# Revit family: Heater-BERKO-Explosion_Proof_Unit
name_source: partatom
category: Mechanical Equipment
units: mm (PartAtom-declared; Revit-internal decimal feet)

## family parameters
Classification = None
Cut with Voids When Loaded = No
Host = Face
Part Type = Normal
Room Calculation Point = No
Round Connector Dimension = Use Diameter
Shared = No

## types (67) — shared parameters
Default Elevation = 4' - 0"
Description = Proof Unit Heater
Frame Size 1 = Yes
Instruction Sheet Link = https://www.marleymep.com
Manufacturer = Marley® Engineered Products
Material = Berko - Stainless Steel - Beige
Number of Poles = 1
Power Factor = 1
Product Documentation Link = https://www.marleymep.com
Product Name = RUX Series Explosion-Proof Unit Heater Gen2
Product Page URL = https://www.marleymep.com
URL = https://www.marleymep.com
Version = 2020 - v1.0a

## per-type parameters (varying)
| type | Actual Supply Air Flow | Air Flow - Throw | Amps | Classification | Depth | Fan Blade Diameter | Frame Size 2 | Frame Size 3 | Frequency | Height | Length | MH Height | MW Height | Motor HP | Motor RPM | Phase | Shipping Weight | Total Heating Capacity | Voltage | Watts |
| RUX-233-FA-0036C | 650 CFM | 1' - 3" | 17 A | 60 Hz Models/Class I, Divisions 1 and 2, Groups C & D/Class II, Divisions 1 and 2, Groups E, F & G/Class I, Zones 1 and 2, Group II | 1' - 4 1/16" | 1' - 0" | No | No | 60 Hz | 1' - 7 3/8" | 1' - 9 3/4" | 0' - 11 1/16" | 0' - 9" | 0.25 | 1725 RPM | 1 | 130 lbs | 10236.0 Btu/h | 208 V | 3000 W |
| RUX-233-FA-0036J | 650 CFM | 1' - 3" | 15 A | 60 Hz Models/Class I, Divisions 1 and 2, Groups C & D/Class II, Divisions 1 and 2, Groups E, F & G/Class I, Zones 1 and 2, Group II | 1' - 4 1/16" | 1' - 0" | No | No | 60 Hz | 1' - 7 3/8" | 1' - 9 3/4" | 0' - 11 1/16" | 0' - 9" | 0.25 | 1725 RPM | 1 | 130 lbs | 10236.0 Btu/h | 240 V | 3000 W |
| RUX-233-FA-0036D | 650 CFM | 1' - 3" | 10 A | 60 Hz Models/Class I, Divisions 1 and 2, Groups C & D/Class II, Divisions 1 and 2, Groups E, F & G/Class I, Zones 1 and 2, Group II | 1' - 4 1/16" | 1' - 0" | No | No | 60 Hz | 1' - 7 3/8" | 1' - 9 3/4" | 0' - 11 1/16" | 0' - 9" | 0.25 | 1725 RPM | 3 | 130 lbs | 10236.0 Btu/h | 208 V | 3000 W |
| RUX-233-FA-0036K | 650 CFM | 1' - 3" | 9 A | 60 Hz Models/Class I, Divisions 1 and 2, Groups C & D/Class II, Divisions 1 and 2, Groups E, F & G/Class I, Zones 1 and 2, Group II | 1' - 4 1/16" | 1' - 0" | No | No | 60 Hz | 1' - 7 3/8" | 1' - 9 3/4" | 0' - 11 1/16" | 0' - 9" | 0.25 | 1725 RPM | 3 | 130 lbs | 10236.0 Btu/h | 240 V | 3000 W |
| RUX-233-FA-0036U | 650 CFM | 1' - 3" | 5 A | 60 Hz Models/Class I, Divisions 1 and 2, Groups C & D/Class II, Divisions 1 and 2, Groups E, F & G/Class I, Zones 1 and 2, Group II | 1' - 4 1/16" | 1' - 0" | No | No | 60 Hz | 1' - 7 3/8" | 1' - 9 3/4" | 0' - 11 1/16" | 0' - 9" | 0.25 | 1725 RPM | 3 | 130 lbs | 10236.0 Btu/h | 480 V | 3000 W |
| RUX-233-FA-0036Z | 650 CFM | 1' - 3" | 4 A | 60 Hz Models/Class I, Divisions 1 and 2, Groups C & D/Class II, Divisions 1 and 2, Groups E, F & G/Class I, Zones 1 and 2, Group II | 1' - 4 1/16" | 1' - 0" | No | No | 60 Hz | 1' - 7 3/8" | 1' - 9 3/4" | 0' - 11 1/16" | 0' - 9" | 0.25 | 1725 RPM | 3 | 130 lbs | 10236.0 Btu/h | 600 V | 3000 W |
| RUX-233-FA-0056C | 650 CFM | 1' - 3" | 26 A | 60 Hz Models/Class I, Divisions 1 and 2, Groups C & D/Class II, Divisions 1 and 2, Groups E, F & G/Class I, Zones 1 and 2, Group II | 1' - 4 1/16" | 1' - 0" | No | No | 60 Hz | 1' - 7 3/8" | 1' - 9 3/4" | 0' - 11 1/16" | 0' - 9" | 0.25 | 1725 RPM | 1 | 130 lbs | 17060.0 Btu/h | 208 V | 5000 W |
| RUX-233-FA-0056J | 650 CFM | 1' - 3" | 23 A | 60 Hz Models/Class I, Divisions 1 and 2, Groups C & D/Class II, Divisions 1 and 2, Groups E, F & G/Class I, Zones 1 and 2, Group II | 1' - 4 1/16" | 1' - 0" | No | No | 60 Hz | 1' - 7 3/8" | 1' - 9 3/4" | 0' - 11 1/16" | 0' - 9" | 0.25 | 1725 RPM | 1 | 130 lbs | 17060.0 Btu/h | 240 V | 5000 W |
| RUX-233-FA-0056D | 650 CFM | 1' - 3" | 16 A | 60 Hz Models/Class I, Divisions 1 and 2, Groups C & D/Class II, Divisions 1 and 2, Groups E, F & G/Class I, Zones 1 and 2, Group II | 1' - 4 1/16" | 1' - 0" | No | No | 60 Hz | 1' - 7 3/8" | 1' - 9 3/4" | 0' - 11 1/16" | 0' - 9" | 0.25 | 1725 RPM | 3 | 130 lbs | 17060.0 Btu/h | 208 V | 5000 W |
| RUX-233-FA-0056K | 650 CFM | 1' - 3" | 14 A | 60 Hz Models/Class I, Divisions 1 and 2, Groups C & D/Class II, Divisions 1 and 2, Groups E, F & G/Class I, Zones 1 and 2, Group II | 1' - 4 1/16" | 1' - 0" | No | No | 60 Hz | 1' - 7 3/8" | 1' - 9 3/4" | 0' - 11 1/16" | 0' - 9" | 0.25 | 1725 RPM | 3 | 130 lbs | 17060.0 Btu/h | 240 V | 5000 W |
| RUX-233-FA-0056U | 650 CFM | 1' - 3" | 7 A | 60 Hz Models/Class I, Divisions 1 and 2, Groups C & D/Class II, Divisions 1 and 2, Groups E, F & G/Class I, Zones 1 and 2, Group II | 1' - 4 1/16" | 1' - 0" | No | No | 60 Hz | 1' - 7 3/8" | 1' - 9 3/4" | 0' - 11 1/16" | 0' - 9" | 0.25 | 1725 RPM | 3 | 130 lbs | 17060.0 Btu/h | 480 V | 5000 W |
| RUX-233-FA-0056Z | 650 CFM | 1' - 3" | 6 A | 60 Hz Models/Class I, Divisions 1 and 2, Groups C & D/Class II, Divisions 1 and 2, Groups E, F & G/Class I, Zones 1 and 2, Group II | 1' - 4 1/16" | 1' - 0" | No | No | 60 Hz | 1' - 7 3/8" | 1' - 9 3/4" | 0' - 11 1/16" | 0' - 9" | 0.25 | 1725 RPM | 3 | 130 lbs | 17060.0 Btu/h | 600 V | 5000 W |
| RUX-233-FA-0086C | 850 CFM | 2' - 1" | 38 A | 60 Hz Models/Class I, Divisions 1 and 2, Groups C & D/Class II, Divisions 1 and 2, Groups E, F & G/Class I, Zones 1 and 2, Group II | 1' - 4 1/16" | 1' - 0" | No | No | 60 Hz | 1' - 7 3/8" | 1' - 9 3/4" | 0' - 11 1/16" | 0' - 9" | 0.25 | 1725 RPM | 1 | 130 lbs | 25590.0 Btu/h | 208 V | 7500 W |
| RUX-233-FA-0086J | 850 CFM | 2' - 1" | 34 A | 60 Hz Models/Class I, Divisions 1 and 2, Groups C & D/Class II, Divisions 1 and 2, Groups E, F & G/Class I, Zones 1 and 2, Group II | 1' - 4 1/16" | 1' - 0" | No | No | 60 Hz | 1' - 7 3/8" | 1' - 9 3/4" | 0' - 11 1/16" | 0' - 9" | 0.25 | 1725 RPM | 1 | 130 lbs | 25590.0 Btu/h | 240 V | 7500 W |
| RUX-233-FA-0086D | 850 CFM | 2' - 1" | 23 A | 60 Hz Models/Class I, Divisions 1 and 2, Groups C & D/Class II, Divisions 1 and 2, Groups E, F & G/Class I, Zones 1 and 2, Group II | 1' - 4 1/16" | 1' - 0" | No | No | 60 Hz | 1' - 7 3/8" | 1' - 9 3/4" | 0' - 11 1/16" | 0' - 9" | 0.25 | 1725 RPM | 3 | 130 lbs | 25590.0 Btu/h | 208 V | 7500 W |
| RUX-233-FA-0086K | 850 CFM | 2' - 1" | 20 A | 60 Hz Models/Class I, Divisions 1 and 2, Groups C & D/Class II, Divisions 1 and 2, Groups E, F & G/Class I, Zones 1 and 2, Group II | 1' - 4 1/16" | 1' - 0" | No | No | 60 Hz | 1' - 7 3/8" | 1' - 9 3/4" | 0' - 11 1/16" | 0' - 9" | 0.25 | 1725 RPM | 3 | 130 lbs | 25590.0 Btu/h | 240 V | 7500 W |
| RUX-233-FA-0086U | 850 CFM | 2' - 1" | 10 A | 60 Hz Models/Class I, Divisions 1 and 2, Groups C & D/Class II, Divisions 1 and 2, Groups E, F & G/Class I, Zones 1 and 2, Group II | 1' - 4 1/16" | 1' - 0" | No | No | 60 Hz | 1' - 7 3/8" | 1' - 9 3/4" | 0' - 11 1/16" | 0' - 9" | 0.25 | 1725 RPM | 3 | 130 lbs | 25590.0 Btu/h | 480 V | 7500 W |
| RUX-233-FA-0086Z | 850 CFM | 2' - 1" | 9 A | 60 Hz Models/Class I, Divisions 1 and 2, Groups C & D/Class II, Divisions 1 and 2, Groups E, F & G/Class I, Zones 1 and 2, Group II | 1' - 4 1/16" | 1' - 0" | No | No | 60 Hz | 1' - 7 3/8" | 1' - 9 3/4" | 0' - 11 1/16" | 0' - 9" | 0.25 | 1725 RPM | 3 | 130 lbs | 25590.0 Btu/h | 600 V | 7500 W |
| RUX-233-FA-0106J | 850 CFM | 2' - 1" | 44 A | 60 Hz Models/Class I, Divisions 1 and 2, Groups C & D/Class II, Divisions 1 and 2, Groups E, F & G/Class I, Zones 1 and 2, Group II | 1' - 4 1/16" | 1' - 0" | No | No | 60 Hz | 1' - 7 3/8" | 1' - 9 3/4" | 0' - 11 1/16" | 0' - 9" | 0.25 | 1725 RPM | 1 | 130 lbs | 34120.0 Btu/h | 240 V | 10000 W |
| RUX-233-FA-0106D | 850 CFM | 2' - 1" | 30 A | 60 Hz Models/Class I, Divisions 1 and 2, Groups C & D/Class II, Divisions 1 and 2, Groups E, F & G/Class I, Zones 1 and 2, Group II | 1' - 4 1/16" | 1' - 0" | No | No | 60 Hz | 1' - 7 3/8" | 1' - 9 3/4" | 0' - 11 1/16" | 0' - 9" | 0.25 | 1725 RPM | 3 | 130 lbs | 34120.0 Btu/h | 208 V | 10000 W |
| RUX-233-FA-0106K | 850 CFM | 2' - 1" | 26 A | 60 Hz Models/Class I, Divisions 1 and 2, Groups C & D/Class II, Divisions 1 and 2, Groups E, F & G/Class I, Zones 1 and 2, Group II | 1' - 4 1/16" | 1' - 0" | No | No | 60 Hz | 1' - 7 3/8" | 1' - 9 3/4" | 0' - 11 1/16" | 0' - 9" | 0.25 | 1725 RPM | 3 | 130 lbs | 34120.0 Btu/h | 240 V | 10000 W |
| RUX-233-FA-0106U | 850 CFM | 2' - 1" | 13 A | 60 Hz Models/Class I, Divisions 1 and 2, Groups C & D/Class II, Divisions 1 and 2, Groups E, F & G/Class I, Zones 1 and 2, Group II | 1' - 4 1/16" | 1' - 0" | No | No | 60 Hz | 1' - 7 3/8" | 1' - 9 3/4" | 0' - 11 1/16" | 0' - 9" | 0.25 | 1725 RPM | 3 | 130 lbs | 34120.0 Btu/h | 480 V | 10000 W |
| RUX-233-FA-0106Z | 850 CFM | 2' - 1" | 11 A | 60 Hz Models/Class I, Divisions 1 and 2, Groups C & D/Class II, Divisions 1 and 2, Groups E, F & G/Class I, Zones 1 and 2, Group II | 1' - 4 1/16" | 1' - 0" | No | No | 60 Hz | 1' - 7 3/8" | 1' - 9 3/4" | 0' - 11 1/16" | 0' - 9" | 0.25 | 1725 RPM | 3 | 130 lbs | 34120.0 Btu/h | 600 V | 10000 W |
| RUX-233-FB-0156D | 1800 CFM | 3' - 9" | 44 A | 60 Hz Models/Class I, Divisions 1 and 2, Groups C & D/Class II, Divisions 1 and 2, Groups E, F & G/Class I, Zones 1 and 2, Group II | 1' - 8 3/16" | 1' - 4" | Yes | No | 60 Hz | 1' - 11 3/8" | 1' - 9 3/4" | 1' - 3 1/16" | 0' - 7" | 0.25 | 1725 RPM | 3 | 169 lbs | 51182.0 Btu/h | 208 V | 15000 W |
| RUX-233-FB-0156K | 1800 CFM | 3' - 9" | 38 A | 60 Hz Models/Class I, Divisions 1 and 2, Groups C & D/Class II, Divisions 1 and 2, Groups E, F & G/Class I, Zones 1 and 2, Group II | 1' - 8 3/16" | 1' - 4" | Yes | No | 60 Hz | 1' - 11 3/8" | 1' - 9 3/4" | 1' - 3 1/16" | 0' - 7" | 0.25 | 1725 RPM | 3 | 169 lbs | 51182.0 Btu/h | 240 V | 15000 W |
| RUX-233-FB-0156U | 1800 CFM | 3' - 9" | 19 A | 60 Hz Models/Class I, Divisions 1 and 2, Groups C & D/Class II, Divisions 1 and 2, Groups E, F & G/Class I, Zones 1 and 2, Group II | 1' - 8 3/16" | 1' - 4" | Yes | No | 60 Hz | 1' - 11 3/8" | 1' - 9 3/4" | 1' - 3 1/16" | 0' - 7" | 0.25 | 1725 RPM | 3 | 169 lbs | 51182.0 Btu/h | 480 V | 15000 W |
| RUX-233-FB-0156Z | 1800 CFM | 3' - 9" | 16 A | 60 Hz Models/Class I, Divisions 1 and 2, Groups C & D/Class II, Divisions 1 and 2, Groups E, F & G/Class I, Zones 1 and 2, Group II | 1' - 8 3/16" | 1' - 4" | Yes | No | 60 Hz | 1' - 11 3/8" | 1' - 9 3/4" | 1' - 3 1/16" | 0' - 7" | 0.25 | 1725 RPM | 3 | 169 lbs | 51182.0 Btu/h | 600 V | 15000 W |
| RUX-233-FB-0206U | 1800 CFM | 3' - 9" | 25 A | 60 Hz Models/Class I, Divisions 1 and 2, Groups C & D/Class II, Divisions 1 and 2, Groups E, F & G/Class I, Zones 1 and 2, Group II | 1' - 8 3/16" | 1' - 4" | Yes | No | 60 Hz | 1' - 11 3/8" | 1' - 9 3/4" | 1' - 3 1/16" | 0' - 7" | 0.25 | 1725 RPM | 3 | 169 lbs | 68242.0 Btu/h | 480 V | 20000 W |
| RUX-233-FB-0206Z | 1800 CFM | 3' - 9" | 21 A | 60 Hz Models/Class I, Divisions 1 and 2, Groups C & D/Class II, Divisions 1 and 2, Groups E, F & G/Class I, Zones 1 and 2, Group II | 1' - 8 3/16" | 1' - 4" | Yes | No | 60 Hz | 1' - 11 3/8" | 1' - 9 3/4" | 1' - 3 1/16" | 0' - 7" | 0.25 | 1725 RPM | 3 | 169 lbs | 68242.0 Btu/h | 600 V | 20000 W |
| RUX-233-FC-0256U | 3110 CFM | 5' - 5" | 31 A | 60 Hz Models/Class I, Divisions 1 and 2, Groups C & D/Class II, Divisions 1 and 2, Groups E, F & G/Class I, Zones 1 and 2, Group II | 2' - 0 3/16" | 1' - 8" | No | Yes | 60 Hz | 2' - 3 3/8" | 1' - 10 3/4" | 1' - 7 1/16" | 0' - 5" | 0.5 | 1725 RPM | 3 | 216 lbs | 85303.0 Btu/h | 480 V | 25000 W |
| RUX-233-FC-0256Z | 3110 CFM | 5' - 5" | 25 A | 60 Hz Models/Class I, Divisions 1 and 2, Groups C & D/Class II, Divisions 1 and 2, Groups E, F & G/Class I, Zones 1 and 2, Group II | 2' - 0 3/16" | 1' - 8" | No | Yes | 60 Hz | 2' - 3 3/8" | 1' - 10 3/4" | 1' - 7 1/16" | 0' - 5" | 0.5 | 1725 RPM | 3 | 216 lbs | 85303.0 Btu/h | 600 V | 25000 W |
| RUX-233-FC-0306U | 3850 CFM | 6' - 3" | 37 A | 60 Hz Models/Class I, Divisions 1 and 2, Groups C & D/Class II, Divisions 1 and 2, Groups E, F & G/Class I, Zones 1 and 2, Group II | 2' - 0 3/16" | 1' - 8" | No | Yes | 60 Hz | 2' - 3 3/8" | 1' - 10 3/4" | 1' - 7 1/16" | 0' - 5" | 0.5 | 1725 RPM | 3 | 216 lbs | 102364.0 Btu/h | 480 V | 30000 W |
| RUX-233-FC-0306Z | 3850 CFM | 6' - 3" | 30 A | 60 Hz Models/Class I, Divisions 1 and 2, Groups C & D/Class II, Divisions 1 and 2, Groups E, F & G/Class I, Zones 1 and 2, Group II | 2' - 0 3/16" | 1' - 8" | No | Yes | 60 Hz | 2' - 3 3/8" | 1' - 10 3/4" | 1' - 7 1/16" | 0' - 5" | 0.5 | 1725 RPM | 3 | 216 lbs | 102364.0 Btu/h | 600 V | 30000 W |
| RUX-233-FA-0036E | 550 CFM | 1' - 1" | 14 A | 50 Hz Models/Class I, Divisions 1 and 2, Groups C & D/Class II, Divisions 1 and 2, Groups E, F & G/Class I, Zones 1 and 2, Group II | 1' - 4 1/16" | 1' - 0" | No | No | 50 Hz | 1' - 7 3/8" | 1' - 9 3/4" | 0' - 11 1/16" | 0' - 9" | 0.25 | 1438 RPM | 1 | 130 lbs | 8530.0 Btu/h | 220 V | 2500 W |
| RUX-233-FA-0036F | 550 CFM | 1' - 1" | 9 A | 50 Hz Models/Class I, Divisions 1 and 2, Groups C & D/Class II, Divisions 1 and 2, Groups E, F & G/Class I, Zones 1 and 2, Group II | 1' - 4 1/16" | 1' - 0" | No | No | 50 Hz | 1' - 7 3/8" | 1' - 9 3/4" | 0' - 11 1/16" | 0' - 9" | 0.25 | 1438 RPM | 3 | 130 lbs | 8530.0 Btu/h | 220 V | 2500 W |
| RUX-233-FA-0036G | 550 CFM | 1' - 1" | 6 A | 50 Hz Models/Class I, Divisions 1 and 2, Groups C & D/Class II, Divisions 1 and 2, Groups E, F & G/Class I, Zones 1 and 2, Group II | 1' - 4 1/16" | 1' - 0" | No | No | 50 Hz | 1' - 7 3/8" | 1' - 9 3/4" | 0' - 11 1/16" | 0' - 9" | 0.25 | 1438 RPM | 3 | 130 lbs | 8530.0 Btu/h | 380 V | 2500 W |
| RUX-233-FA-0036H | 550 CFM | 1' - 1" | 6 A | 50 Hz Models/Class I, Divisions 1 and 2, Groups C & D/Class II, Divisions 1 and 2, Groups E, F & G/Class I, Zones 1 and 2, Group II | 1' - 4 1/16" | 1' - 0" | No | No | 50 Hz | 1' - 7 3/8" | 1' - 9 3/4" | 0' - 11 1/16" | 0' - 9" | 0.25 | 1438 RPM | 3 | 130 lbs | 8530.0 Btu/h | 400 V | 2500 W |
| RUX-233-FA-0036I | 550 CFM | 1' - 1" | 5 A | 50 Hz Models/Class I, Divisions 1 and 2, Groups C & D/Class II, Divisions 1 and 2, Groups E, F & G/Class I, Zones 1 and 2, Group II | 1' - 4 1/16" | 1' - 0" | No | No | 50 Hz | 1' - 7 3/8" | 1' - 9 3/4" | 0' - 11 1/16" | 0' - 9" | 0.25 | 1438 RPM | 3 | 130 lbs | 8530.0 Btu/h | 415 V | 2500 W |
| RUX-233-FA-0056E | 550 CFM | 1' - 1" | 21 A | 50 Hz Models/Class I, Divisions 1 and 2, Groups C & D/Class II, Divisions 1 and 2, Groups E, F & G/Class I, Zones 1 and 2, Group II | 1' - 4 1/16" | 1' - 0" | No | No | 50 Hz | 1' - 7 3/8" | 1' - 9 3/4" | 0' - 11 1/16" | 0' - 9" | 0.25 | 1438 RPM | 1 | 130 lbs | 14330.0 Btu/h | 220 V | 4200 W |
| RUX-233-FA-0056F | 550 CFM | 1' - 1" | 12 A | 50 Hz Models/Class I, Divisions 1 and 2, Groups C & D/Class II, Divisions 1 and 2, Groups E, F & G/Class I, Zones 1 and 2, Group II | 1' - 4 1/16" | 1' - 0" | No | No | 50 Hz | 1' - 7 3/8" | 1' - 9 3/4" | 0' - 11 1/16" | 0' - 9" | 0.25 | 1438 RPM | 3 | 130 lbs | 14330.0 Btu/h | 220 V | 4200 W |
| RUX-233-FA-0056G | 550 CFM | 1' - 1" | 9 A | 50 Hz Models/Class I, Divisions 1 and 2, Groups C & D/Class II, Divisions 1 and 2, Groups E, F & G/Class I, Zones 1 and 2, Group II | 1' - 4 1/16" | 1' - 0" | No | No | 50 Hz | 1' - 7 3/8" | 1' - 9 3/4" | 0' - 11 1/16" | 0' - 9" | 0.25 | 1438 RPM | 3 | 130 lbs | 14330.0 Btu/h | 380 V | 4200 W |
| RUX-233-FA-0056H | 550 CFM | 1' - 1" | 8 A | 50 Hz Models/Class I, Divisions 1 and 2, Groups C & D/Class II, Divisions 1 and 2, Groups E, F & G/Class I, Zones 1 and 2, Group II | 1' - 4 1/16" | 1' - 0" | No | No | 50 Hz | 1' - 7 3/8" | 1' - 9 3/4" | 0' - 11 1/16" | 0' - 9" | 0.25 | 1438 RPM | 3 | 130 lbs | 14330.0 Btu/h | 400 V | 4200 W |
| RUX-233-FA-0056I | 550 CFM | 1' - 1" | 7 A | 50 Hz Models/Class I, Divisions 1 and 2, Groups C & D/Class II, Divisions 1 and 2, Groups E, F & G/Class I, Zones 1 and 2, Group II | 1' - 4 1/16" | 1' - 0" | No | No | 50 Hz | 1' - 7 3/8" | 1' - 9 3/4" | 0' - 11 1/16" | 0' - 9" | 0.25 | 1438 RPM | 3 | 130 lbs | 14330.0 Btu/h | 415 V | 4200 W |
| RUX-233-FA-0076E | 700 CFM | 1' - 10" | 31 A | 50 Hz Models/Class I, Divisions 1 and 2, Groups C & D/Class II, Divisions 1 and 2, Groups E, F & G/Class I, Zones 1 and 2, Group II | 1' - 4 1/16" | 1' - 0" | No | No | 50 Hz | 1' - 7 3/8" | 1' - 9 3/4" | 0' - 11 1/16" | 0' - 9" | 0.25 | 1438 RPM | 1 | 130 lbs | 21496.0 Btu/h | 220 V | 6300 W |
| RUX-233-FA-0076F | 700 CFM | 1' - 10" | 19 A | 50 Hz Models/Class I, Divisions 1 and 2, Groups C & D/Class II, Divisions 1 and 2, Groups E, F & G/Class I, Zones 1 and 2, Group II | 1' - 4 1/16" | 1' - 0" | No | No | 50 Hz | 1' - 7 3/8" | 1' - 9 3/4" | 0' - 11 1/16" | 0' - 9" | 0.25 | 1438 RPM | 3 | 130 lbs | 21496.0 Btu/h | 220 V | 6300 W |
| RUX-233-FA-0076G | 700 CFM | 1' - 10" | 12 A | 50 Hz Models/Class I, Divisions 1 and 2, Groups C & D/Class II, Divisions 1 and 2, Groups E, F & G/Class I, Zones 1 and 2, Group II | 1' - 4 1/16" | 1' - 0" | No | No | 50 Hz | 1' - 7 3/8" | 1' - 9 3/4" | 0' - 11 1/16" | 0' - 9" | 0.25 | 1438 RPM | 3 | 130 lbs | 21496.0 Btu/h | 380 V | 6300 W |
| RUX-233-FA-0076H | 700 CFM | 1' - 10" | 11 A | 50 Hz Models/Class I, Divisions 1 and 2, Groups C & D/Class II, Divisions 1 and 2, Groups E, F & G/Class I, Zones 1 and 2, Group II | 1' - 4 1/16" | 1' - 0" | No | No | 50 Hz | 1' - 7 3/8" | 1' - 9 3/4" | 0' - 11 1/16" | 0' - 9" | 0.25 | 1438 RPM | 3 | 130 lbs | 21496.0 Btu/h | 400 V | 6300 W |
| RUX-233-FA-0076I | 700 CFM | 1' - 10" | 10 A | 50 Hz Models/Class I, Divisions 1 and 2, Groups C & D/Class II, Divisions 1 and 2, Groups E, F & G/Class I, Zones 1 and 2, Group II | 1' - 4 1/16" | 1' - 0" | No | No | 50 Hz | 1' - 7 3/8" | 1' - 9 3/4" | 0' - 11 1/16" | 0' - 9" | 0.25 | 1438 RPM | 3 | 130 lbs | 21496.0 Btu/h | 415 V | 6300 W |
| RUX-233-FA-0096E | 700 CFM | 1' - 10" | 40 A | 50 Hz Models/Class I, Divisions 1 and 2, Groups C & D/Class II, Divisions 1 and 2, Groups E, F & G/Class I, Zones 1 and 2, Group II | 1' - 4 1/16" | 1' - 0" | No | No | 50 Hz | 1' - 7 3/8" | 1' - 9 3/4" | 0' - 11 1/16" | 0' - 9" | 0.25 | 1438 RPM | 1 | 130 lbs | 28660.0 Btu/h | 220 V | 8400 W |
| RUX-233-FA-0096F | 700 CFM | 1' - 10" | 24 A | 50 Hz Models/Class I, Divisions 1 and 2, Groups C & D/Class II, Divisions 1 and 2, Groups E, F & G/Class I, Zones 1 and 2, Group II | 1' - 4 1/16" | 1' - 0" | No | No | 50 Hz | 1' - 7 3/8" | 1' - 9 3/4" | 0' - 11 1/16" | 0' - 9" | 0.25 | 1438 RPM | 3 | 130 lbs | 28660.0 Btu/h | 220 V | 8400 W |
| RUX-233-FA-0096G | 700 CFM | 1' - 10" | 15 A | 50 Hz Models/Class I, Divisions 1 and 2, Groups C & D/Class II, Divisions 1 and 2, Groups E, F & G/Class I, Zones 1 and 2, Group II | 1' - 4 1/16" | 1' - 0" | No | No | 50 Hz | 1' - 7 3/8" | 1' - 9 3/4" | 0' - 11 1/16" | 0' - 9" | 0.25 | 1438 RPM | 3 | 130 lbs | 28660.0 Btu/h | 380 V | 8400 W |
| RUX-233-FA-0096H | 700 CFM | 1' - 10" | 13 A | 50 Hz Models/Class I, Divisions 1 and 2, Groups C & D/Class II, Divisions 1 and 2, Groups E, F & G/Class I, Zones 1 and 2, Group II | 1' - 4 1/16" | 1' - 0" | No | No | 50 Hz | 1' - 7 3/8" | 1' - 9 3/4" | 0' - 11 1/16" | 0' - 9" | 0.25 | 1438 RPM | 3 | 130 lbs | 28660.0 Btu/h | 400 V | 8400 W |
| RUX-233-FA-0096I | 700 CFM | 1' - 10" | 13 A | 50 Hz Models/Class I, Divisions 1 and 2, Groups C & D/Class II, Divisions 1 and 2, Groups E, F & G/Class I, Zones 1 and 2, Group II | 1' - 4 1/16" | 1' - 0" | No | No | 50 Hz | 1' - 7 3/8" | 1' - 9 3/4" | 0' - 11 1/16" | 0' - 9" | 0.25 | 1438 RPM | 3 | 130 lbs | 28660.0 Btu/h | 415 V | 8400 W |
| RUX-233-FB-0136F | 1500 CFM | 3' - 3" | 35 A | 50 Hz Models/Class I, Divisions 1 and 2, Groups C & D/Class II, Divisions 1 and 2, Groups E, F & G/Class I, Zones 1 and 2, Group II | 1' - 8 3/16" | 1' - 4" | Yes | No | 50 Hz | 1' - 11 3/8" | 1' - 9 3/4" | 1' - 3 1/16" | 0' - 7" | 0.25 | 1438 RPM | 3 | 169 lbs | 42650.0 Btu/h | 220 V | 12500 W |
| RUX-233-FB-0136G | 1500 CFM | 3' - 3" | 21 A | 50 Hz Models/Class I, Divisions 1 and 2, Groups C & D/Class II, Divisions 1 and 2, Groups E, F & G/Class I, Zones 1 and 2, Group II | 1' - 8 3/16" | 1' - 4" | Yes | No | 50 Hz | 1' - 11 3/8" | 1' - 9 3/4" | 1' - 3 1/16" | 0' - 7" | 0.25 | 1438 RPM | 3 | 169 lbs | 42650.0 Btu/h | 380 V | 12500 W |
| RUX-233-FB-0136H | 1500 CFM | 3' - 3" | 19 A | 50 Hz Models/Class I, Divisions 1 and 2, Groups C & D/Class II, Divisions 1 and 2, Groups E, F & G/Class I, Zones 1 and 2, Group II | 1' - 8 3/16" | 1' - 4" | Yes | No | 50 Hz | 1' - 11 3/8" | 1' - 9 3/4" | 1' - 3 1/16" | 0' - 7" | 0.25 | 1438 RPM | 3 | 169 lbs | 42650.0 Btu/h | 400 V | 12500 W |
| RUX-233-FB-0136I | 1500 CFM | 3' - 3" | 18 A | 50 Hz Models/Class I, Divisions 1 and 2, Groups C & D/Class II, Divisions 1 and 2, Groups E, F & G/Class I, Zones 1 and 2, Group II | 1' - 8 3/16" | 1' - 4" | Yes | No | 50 Hz | 1' - 11 3/8" | 1' - 9 3/4" | 1' - 3 1/16" | 0' - 7" | 0.25 | 1438 RPM | 3 | 169 lbs | 42650.0 Btu/h | 415 V | 12500 W |
| RUX-233-FB-0176F | 1500 CFM | 3' - 3" | 46 A | 50 Hz Models/Class I, Divisions 1 and 2, Groups C & D/Class II, Divisions 1 and 2, Groups E, F & G/Class I, Zones 1 and 2, Group II | 1' - 8 3/16" | 1' - 4" | Yes | No | 50 Hz | 1' - 11 3/8" | 1' - 9 3/4" | 1' - 3 1/16" | 0' - 7" | 0.25 | 1438 RPM | 3 | 169 lbs | 56982.0 Btu/h | 220 V | 16700 W |
| RUX-233-FB-0176G | 1500 CFM | 3' - 3" | 28 A | 50 Hz Models/Class I, Divisions 1 and 2, Groups C & D/Class II, Divisions 1 and 2, Groups E, F & G/Class I, Zones 1 and 2, Group II | 1' - 8 3/16" | 1' - 4" | Yes | No | 50 Hz | 1' - 11 3/8" | 1' - 9 3/4" | 1' - 3 1/16" | 0' - 7" | 0.25 | 1438 RPM | 3 | 169 lbs | 56982.0 Btu/h | 380 V | 16700 W |
| RUX-233-FB-0176H | 1500 CFM | 3' - 3" | 25 A | 50 Hz Models/Class I, Divisions 1 and 2, Groups C & D/Class II, Divisions 1 and 2, Groups E, F & G/Class I, Zones 1 and 2, Group II | 1' - 8 3/16" | 1' - 4" | Yes | No | 50 Hz | 1' - 11 3/8" | 1' - 9 3/4" | 1' - 3 1/16" | 0' - 7" | 0.25 | 1438 RPM | 3 | 169 lbs | 56982.0 Btu/h | 400 V | 16700 W |
| RUX-233-FB-0176I | 1500 CFM | 3' - 3" | 24 A | 50 Hz Models/Class I, Divisions 1 and 2, Groups C & D/Class II, Divisions 1 and 2, Groups E, F & G/Class I, Zones 1 and 2, Group II | 1' - 8 3/16" | 1' - 4" | Yes | No | 50 Hz | 1' - 11 3/8" | 1' - 9 3/4" | 1' - 3 1/16" | 0' - 7" | 0.25 | 1438 RPM | 3 | 169 lbs | 56982.0 Btu/h | 315 V | 16700 W |
| RUX-233-FC-0216G | 2600 CFM | 4' - 9" | 33 A | 50 Hz Models/Class I, Divisions 1 and 2, Groups C & D/Class II, Divisions 1 and 2, Groups E, F & G/Class I, Zones 1 and 2, Group II | 2' - 0 3/16" | 1' - 8" | No | Yes | 50 Hz | 2' - 3 3/8" | 1' - 10 3/4" | 1' - 7 1/16" | 0' - 5" | 0.5 | 1438 RPM | 3 | 216 lbs | 71654.0 Btu/h | 380 V | 21000 W |
| RUX-233-FC-0216H | 2600 CFM | 4' - 9" | 32 A | 50 Hz Models/Class I, Divisions 1 and 2, Groups C & D/Class II, Divisions 1 and 2, Groups E, F & G/Class I, Zones 1 and 2, Group II | 2' - 0 3/16" | 1' - 8" | No | Yes | 50 Hz | 2' - 3 3/8" | 1' - 10 3/4" | 1' - 7 1/16" | 0' - 5" | 0.5 | 1438 RPM | 3 | 216 lbs | 71654.0 Btu/h | 400 V | 21000 W |
| RUX-233-FC-0216I | 2600 CFM | 4' - 9" | 31 A | 50 Hz Models/Class I, Divisions 1 and 2, Groups C & D/Class II, Divisions 1 and 2, Groups E, F & G/Class I, Zones 1 and 2, Group II | 2' - 0 3/16" | 1' - 8" | No | Yes | 50 Hz | 2' - 3 3/8" | 1' - 10 3/4" | 1' - 7 1/16" | 0' - 5" | 0.5 | 1438 RPM | 3 | 216 lbs | 71654.0 Btu/h | 415 V | 21000 W |
| RUX-233-FC-0256G | 2600 CFM | 4' - 9" | 39 A | 50 Hz Models/Class I, Divisions 1 and 2, Groups C & D/Class II, Divisions 1 and 2, Groups E, F & G/Class I, Zones 1 and 2, Group II | 2' - 0 3/16" | 1' - 8" | No | Yes | 50 Hz | 2' - 3 3/8" | 1' - 10 3/4" | 1' - 7 1/16" | 0' - 5" | 0.5 | 1438 RPM | 3 | 216 lbs | 85303.0 Btu/h | 380 V | 25000 W |
| RUX-233-FC-0256H | 2600 CFM | 4' - 9" | 37 A | 50 Hz Models/Class I, Divisions 1 and 2, Groups C & D/Class II, Divisions 1 and 2, Groups E, F & G/Class I, Zones 1 and 2, Group II | 2' - 0 3/16" | 1' - 8" | No | Yes | 50 Hz | 2' - 3 3/8" | 1' - 10 3/4" | 1' - 7 1/16" | 0' - 5" | 0.5 | 1438 RPM | 3 | 216 lbs | 85303.0 Btu/h | 400 V | 25000 W |
| RUX-233-FC-0256I | 2600 CFM | 4' - 9" | 36 A | 50 Hz Models/Class I, Divisions 1 and 2, Groups C & D/Class II, Divisions 1 and 2, Groups E, F & G/Class I, Zones 1 and 2, Group II | 2' - 0 3/16" | 1' - 8" | No | Yes | 50 Hz | 2' - 3 3/8" | 1' - 10 3/4" | 1' - 7 1/16" | 0' - 5" | 0.5 | 1438 RPM | 3 | 216 lbs | 85303.0 Btu/h | 415 V | 25000 W |

note: column(s) folded — value = type name in every type: Model

## geometry (parser evidence)
native form markers: Sweep x3
no freeform markers — native parametric forms only
